# Revit family: Deca_Prateleira Disco_2030.C.DSC
name_source: partatom
category: Plumbing Fixtures
revit_build: Autodesk Revit Architecture 2012 (Build: 20110916_2132(x64)
units: mm (PartAtom-declared; Revit-internal decimal feet)

## types (1)
- 2030.C.DSC_Cromado CR10
    Acessório = Deca VR 12 Branco Vidro
    Aprovado por = Contino/quattroD
    Assembly Code = D2010
    Atendimento ao Cliente = 0800-0117073
    Criado por = Contino/quattroD
    Código = 2030.C.DSC
    Default Elevation = 1100 mm
    Description = Prateleira
    HWFU = 0
    Informações Complementares = Os parafusos e buchas que acompanham o produto devem ser utilzados apenas em paredes de concreto ou tijolo maciço. Para instalações em Drywall, consultar projetista ou engenheiro da obra.
    Linha = Disco
    Louça/Metais = Metal
    Manufacturer = Deca
    Material = Deca_Latão Cromado e Plástico de Engenharia
    Model = 2030.C.DSC
    Norma = ABNT NBR 10283: 2003
    Peso Liquido (Kg) = 0.55
    Produto = Preteleira Disco
    Saboneteira = Deca CR10 Cromado
    Segmento = Médio
    URL = www.deca.com.br/produtos
    Variações de COR = Cromado (2030.C.DSC)

## geometry (parser evidence)
native form markers: Blend x3, Sweep x2
no freeform markers — native parametric forms only
